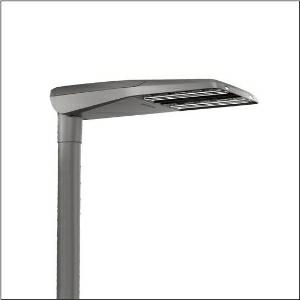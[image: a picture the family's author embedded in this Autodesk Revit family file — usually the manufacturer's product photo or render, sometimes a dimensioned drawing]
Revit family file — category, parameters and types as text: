
# Revit family: streetlight_sl_11_iq_midi___st1_0a_5xc3m41f08le_9450
name_source: partatom
category: Lighting Fixtures
units: mm (PartAtom-declared; Revit-internal decimal feet)

## family parameters
Cut with Voids When Loaded = No
Host = Face
Light Source = No
Part Type = Normal
Room Calculation Point = No
Round Connector Dimension = Use Diameter
Shared = No

## types (1)
- --- (1 x LED, 9290 lm, 60.4 W, 4000K)
    Apparent Load = 60 VA
    CIE Flux Codes = 33 66 96 100 100
    Color Rendering = 70
    Color Temperature = 4000K
    Default Elevation = 1800 mm
    Description = Streetlight SL 11 iQ midi, mast luminaire, primary light control with 3 zone facetted reflector, of plastic, silver coated, highly specular, primary optical cover: cover, of PMMA, transparent, light distribution: ST1.0a, light emission: direct distribution, primary light characteristic: asymmetric, installation type: post-top, side-entry, lamps: LED, High Power LED, rated values: 9.290lm | 60,4W | 153,8lm/W (begin service life); end service life: 9.290lm | 62,5W; at 50% lumin. flux: 4.645lm | 29,7W | 156,4lm/W, colour temperature: 4000K, colour rendering: CRI > 70, light colour: 740, light setting 1 begin service life: 100% | 9.290lm | 60,4W | 153,8lm/W | 4.000K, light setting 1 end service life: 62,5W, further light settings possible, control: optimised constant luminous flux control (CLO 2.0), Street-Remote, Desk-Remote (wireless, voltage-free reading and setting of iQ features in the workshop via application-optimized NFC function/RFID function), Light-Fading, Smart-Wire, Night-Set, Lumen-Switch, Temp-Guard, Auto-Match, with cable H07RN-F 3x 1.5mm², mains connection: 230..240V, AC, 50/60Hz, connection cable pre-assembled, cable length: 8,5m, luminaire housing, of diecast aluminium, powder-coated, SITECO metallic grey (DB 702S), please order mast flange separately, inclination adjustable without tools: 0°, 5°, 10°, 15° (post-top) | 0°, -5°, -10°, -15° (side-entry), sealing non-destructively replaceable, multi-level sealing system, length: 780mm, width: 376mm, height: 118mm, mast flange for spigot size: 42mm (side-entry): 5XC10008XM4, 60/48mm (side-entry/post-top): 5XC10108XM2, 76/60mm (side-entry/post-top): 5XC10108XM1, equipment: standard, protection rating (complete): IP66, insulation class (complete): insulation class II (safety insulation), certification: CE, ENEC, ENEC+, VDE, impact resistance: IK10, permissible operating ambient temperature for outdoor applications: -25..+50°C, standard-compliant lighting for roads and squares, Environmental Product Declaration (EPD) tested and certified by an independent institute, packaging unit: 1 piece

Light Distribution: ST1.0a
    Height = 118 mm
    Lamp = 1 x LED
    Lamp Light Flux = 9290 lm
    Lamp Power = 60.4 W
    Lamp count = 1
    Length = 780 mm
    Luminous efficacy = 154 lm/W
    Manufacturer = Siteco
    ModVariant = No
    Model = 5XC3M41F08LE
    Number of Poles = 1
    OnlyDefault = Yes
    Power Factor = 1
    Product Name = Streetlight SL 11 iQ midi | ST1.0a
    Product group = mast luminaire | pylon top
    ProductGroupID = 6100
    Protection Class = Protection class II
    Protection Degree = IP 66
    RLX_Detail_Level = 1
    RLX_Emergency_Light_Flux = 0 lm
    RLX_Emergency_Type = 0
    RLX_Emergency_Type_DB = No
    RlxData = <blob elided: 70217 chars, md5=78b41fb5>
    Socket = socket
    Standby Power = 0 W
    System Light Flux = 9290 lm
    System Power = 60 W
    Type Comments = factory setting: luminous flux: 100 % | dim-lin: 254 | 520 mA
    Type Image = l_1005960.jpg
    URL = http://relux.com
    VarID = @adj_092455
    Voltage = 0 V
    Weight = 0.00 kg
    Width = 376 mm

## geometry (parser evidence)
native form markers: Blend x4, Sweep x10
no freeform markers — native parametric forms only
